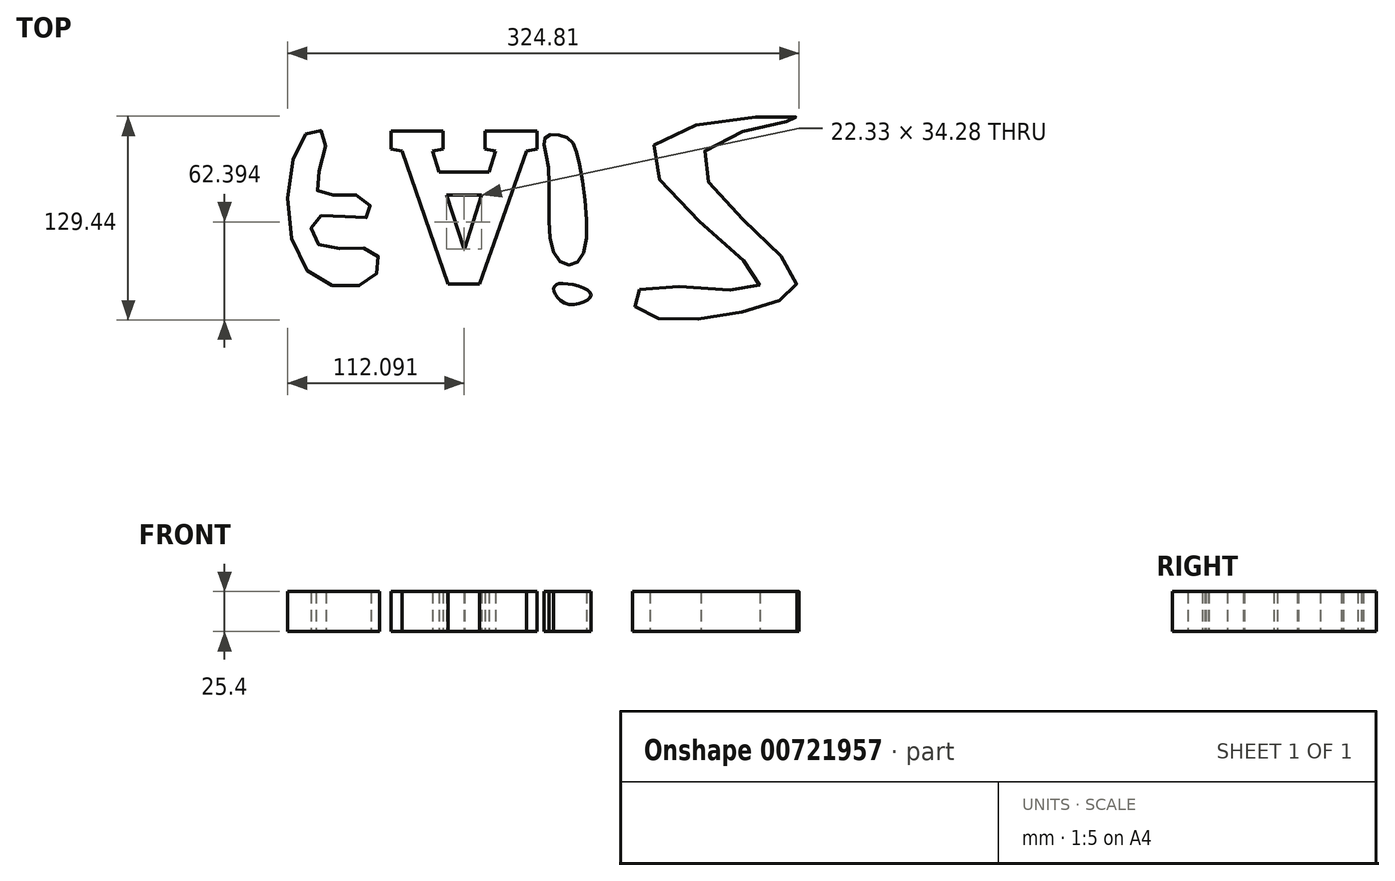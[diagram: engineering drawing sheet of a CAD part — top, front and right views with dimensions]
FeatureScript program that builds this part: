
annotation { "Feature Type Name" : "Feature", "Feature Type Description" : "" }
export const myFeature = defineFeature(function(context is Context, id is Id, definition is map)
    precondition{}
    {
        {
            var Q0;
            Q0=qCreatedBy(makeId("Top.planeOp"),FACE);
            var sketch = newSketch(context, id + "F0", { "sketchPlane" : qUnion([Q0])});
            skFitSpline(sketch, "E0", {"points": [v(101.53, 10.12) * mm, v(106.63, -46.81) * mm, v(121.5, -48.51) * mm, v(121.5, 11.4) * mm, v(112.58, 29.66) * mm, v(99.83, 29.66) * mm, v(101.53, 10.12) * mm]});
            skFitSpline(sketch, "E1", {"points": [v(110.88, -63.38) * mm, v(128.72, -70.6) * mm, v(114.28, -76.55) * mm, v(104.93, -66.78) * mm, v(110.88, -63.38) * mm]});
            skFitSpline(sketch, "E2", {"points": [v(-52.7, 31.36) * mm, v(-53.11, -53.6) * mm, v(-9.78, -59.98) * mm, v(-9.78, -42.56) * mm, v(-44.2, -38.74) * mm, v(-45.47, -21.32) * mm, v(-12.75, -20.9) * mm, v(-17, -8.15) * mm, v(-45.04, -4.75) * mm, v(-39.94, 30.09) * mm, v(-52.7, 31.36) * mm]});
            skText(sketch, "E3", { "text": "A\n", "fontName": "RobotoSlab-Bold.ttf"});
            skFitSpline(sketch, "E4", {"points": [v(159.33, -67.33) * mm, v(235.9, -63.34) * mm, v(166.6, 20.77) * mm, v(260.72, 41.83) * mm, v(199.45, 18.4) * mm, v(258.2, -57.8) * mm, v(234.92, -78.87) * mm, v(159.79, -81.34) * mm, v(159.33, -67.33) * mm]});
            const initialGuessF0  = {"E3": [0.09722, 0.03353, -1, 0, 0.09855]};
            skSetInitialGuess(sketch, initialGuessF0);
            skSolve(sketch);
        }
        {
            var Q0;
            Q0=makeQuery(id+"F0.imprint","IMPRINT",FACE,{"disambiguationData":[TD([[makeQuery(id+"F0.imprint","IMPRINT",EDGE,{"derivedFrom":sQuery(id+"F0.wireOp",EDGE,"E0")}),1.0]])]});
            extrude(context, id + "F1", {"entities" : qUnion([Q0]), "depth" : 25.4 * mm, "offsetDistance" : 25.4 * mm});
        }
        {
            var Q0;
            Q0 = qSketchRegion(id + "F0", true);
            extrude(context, id + "F2", {"entities" : qUnion([Q0]), "operationType" : NewBodyOperationType.ADD, "depth" : 25.4 * mm, "offsetDistance" : 25.4 * mm});
        }
    });
